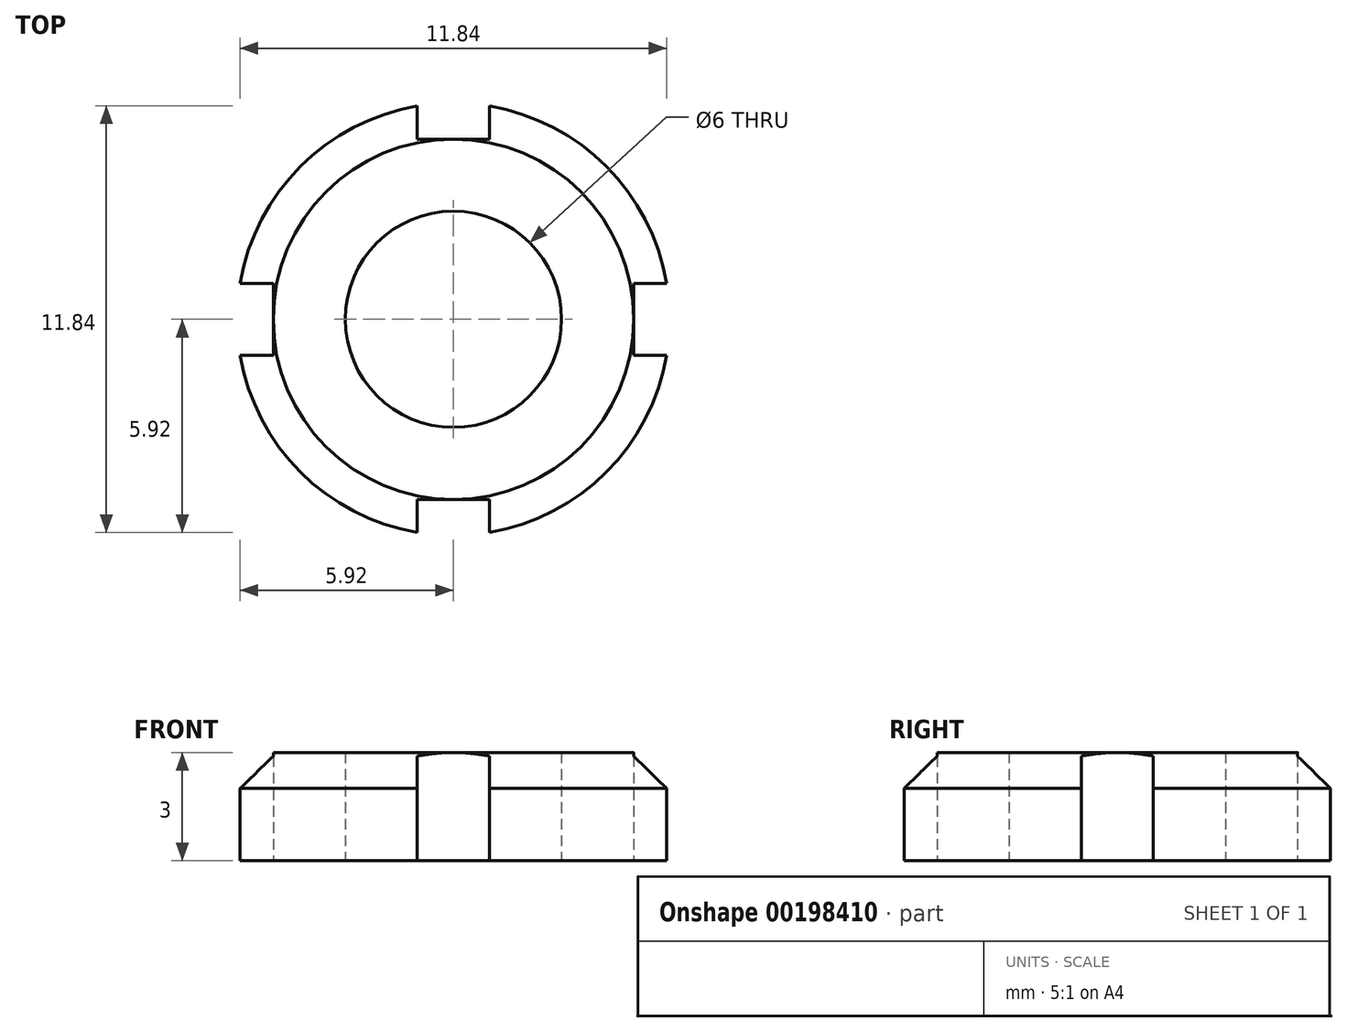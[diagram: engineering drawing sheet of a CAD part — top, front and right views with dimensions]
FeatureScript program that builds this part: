
annotation { "Feature Type Name" : "Feature", "Feature Type Description" : "" }
export const myFeature = defineFeature(function(context is Context, id is Id, definition is map)
    precondition{}
    {
        {
            var Q0;
            Q0=qCreatedBy(makeId("Top.planeOp"),FACE);
            var sketch = newSketch(context, id + "F0", { "sketchPlane" : qUnion([Q0])});
            skArc(sketch, "E0", {"start": v(-1, 5.92) * mm, "mid": v(-4.24, 4.24) * mm, "end": v(-5.92, 1) * mm});
            skCircle(sketch, "E1", {"center": v(0, 0) * mm, "radius": 3 * mm});
            skLineSegment(sketch, "E2.bottom", {"start": v(-1, 5) * mm, "end": v(1, 5) * mm});
            skLineSegment(sketch, "E2.left", {"start": v(-1, 5) * mm, "end": v(-1, 5.92) * mm});
            skLineSegment(sketch, "E2.right", {"start": v(1, 5) * mm, "end": v(1, 5.92) * mm});
            skPoint(sketch, "E2.middle", {"position": v(0, 6) * mm});
            skPoint(sketch, "E3.orphan", {"position": v(1, 7) * mm});
            skPoint(sketch, "E4.orphan", {"position": v(-1, 7) * mm});
            skLineSegment(sketch, "E5.1.0", {"start": v(-5, -1) * mm, "end": v(-5, 1) * mm});
            skLineSegment(sketch, "E5.1.1", {"start": v(-5, 1) * mm, "end": v(-5.92, 1) * mm});
            skLineSegment(sketch, "E5.1.2", {"start": v(-5, -1) * mm, "end": v(-5.92, -1) * mm});
            skLineSegment(sketch, "E5.2.0", {"start": v(1, -5) * mm, "end": v(-1, -5) * mm});
            skLineSegment(sketch, "E5.2.1", {"start": v(-1, -5) * mm, "end": v(-1, -5.92) * mm});
            skLineSegment(sketch, "E5.2.2", {"start": v(1, -5) * mm, "end": v(1, -5.92) * mm});
            skLineSegment(sketch, "E5.3.0", {"start": v(5, 1) * mm, "end": v(5, -1) * mm});
            skLineSegment(sketch, "E5.3.1", {"start": v(5, -1) * mm, "end": v(5.92, -1) * mm});
            skLineSegment(sketch, "E5.3.2", {"start": v(5, 1) * mm, "end": v(5.92, 1) * mm});
            skArc(sketch, "E6.trimOffspring", {"start": v(5.92, 1) * mm, "mid": v(4.24, 4.24) * mm, "end": v(1, 5.92) * mm});
            skArc(sketch, "E7.trimOffspring", {"start": v(-5.92, -1) * mm, "mid": v(-4.24, -4.24) * mm, "end": v(-1, -5.92) * mm});
            skArc(sketch, "E8.trimOffspring", {"start": v(1, -5.92) * mm, "mid": v(4.24, -4.24) * mm, "end": v(5.92, -1) * mm});
            skSolve(sketch);
        }
        {
            var Q0;
            Q0=makeQuery(id+"F0.imprint","IMPRINT",FACE,{"disambiguationData":[TD([[makeQuery(id+"F0.imprint","IMPRINT",EDGE,{"derivedFrom":sQuery(id+"F0.wireOp",EDGE,"E0")}),1.0]])]});
            extrude(context, id + "F1", {"entities" : qUnion([Q0]), "depth" : 3 * mm});
        }
        {
            var Q0;
            Q0=makeQuery(id+"F1.opExtrude","CAP_EDGE",EDGE,{"disambiguationData":[OSD([sQuery(id+"F0.wireOp",EDGE,"E7.trimOffspring")])],"isStart":false});
            var Q1;
            Q1=makeQuery(id+"F1.opExtrude","CAP_EDGE",EDGE,{"disambiguationData":[OSD([sQuery(id+"F0.wireOp",EDGE,"E0")])],"isStart":false});
            var Q2;
            Q2=makeQuery(id+"F1.opExtrude","CAP_EDGE",EDGE,{"disambiguationData":[OSD([sQuery(id+"F0.wireOp",EDGE,"E6.trimOffspring")])],"isStart":false});
            var Q3;
            Q3=makeQuery(id+"F1.opExtrude","CAP_EDGE",EDGE,{"disambiguationData":[OSD([sQuery(id+"F0.wireOp",EDGE,"E8.trimOffspring")])],"isStart":false});
            chamfer(context, id + "F2", {"entities" : qUnion([Q0, Q1, Q2, Q3]), "width" : 1 * mm, "tangentPropagation" : true});
        }
    });
